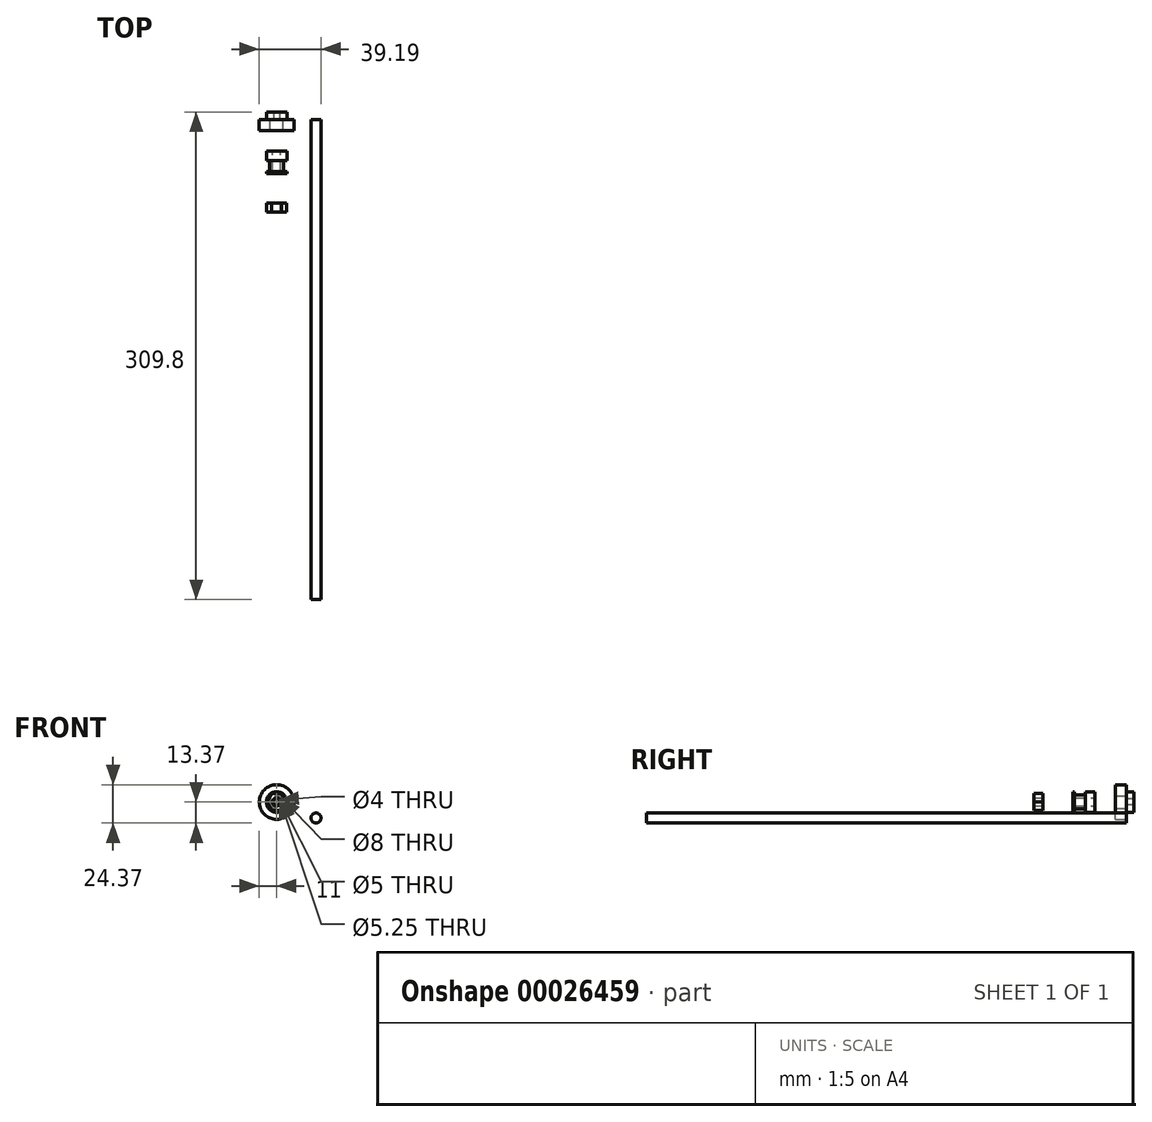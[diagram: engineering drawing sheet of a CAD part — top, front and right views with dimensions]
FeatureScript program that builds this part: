
annotation { "Feature Type Name" : "Feature", "Feature Type Description" : "" }
export const myFeature = defineFeature(function(context is Context, id is Id, definition is map)
    precondition{}
    {
        {
            var Q0;
            Q0=qCreatedBy(makeId("Front.planeOp"),FACE);
            cPlane(context, id + "F0", {"entities" : qUnion([Q0]), "cplaneType" : CPlaneType.OFFSET, "offset" : 20 * mm, "width" : 150 * mm, "height" : 150 * mm});
        }
        {
            var Q0;
            Q0=qCreatedBy(makeId("Front.planeOp"),FACE);
            var sketch = newSketch(context, id + "F1", { "sketchPlane" : qUnion([Q0])});
            skCircle(sketch, "E0", {"center": v(0, 0) * mm, "radius": 4 * mm});
            skCircle(sketch, "E1", {"center": v(0, 0) * mm, "radius": 11 * mm});
            skSolve(sketch);
        }
        {
            var Q0;
            Q0=makeQuery(id+"F1.imprint","IMPRINT",FACE,{"disambiguationData":[TD([[makeQuery(id+"F1.imprint","IMPRINT",EDGE,{"derivedFrom":sQuery(id+"F1.wireOp",EDGE,"E0")}),-1.0]])]});
            var Q1;
            Q1=sQuery(id+"F1.wireOp",EDGE,"E1");
            extrude(context, id + "F14", {"entities" : qUnion([Q0]), "surfaceEntities" : qUnion([Q1]), "depth" : 7 * mm});
        }
        {
            var Q0;
            Q0=qCreatedBy(makeId("Front.planeOp"),FACE);
            var sketch = newSketch(context, id + "F2", { "sketchPlane" : qUnion([Q0])});
            skCircle(sketch, "E2", {"center": v(0, 0) * mm, "radius": 2 * mm});
            skCircle(sketch, "E3", {"center": v(0, 0) * mm, "radius": 6.5 * mm});
            skSolve(sketch);
        }
        {
            var Q0;
            Q0=makeQuery(id+"F2.imprint","IMPRINT",FACE,{"disambiguationData":[TD([[makeQuery(id+"F2.imprint","IMPRINT",EDGE,{"derivedFrom":sQuery(id+"F2.wireOp",EDGE,"E2")}),-1.0]])]});
            extrude(context, id + "F3", {"entities" : qUnion([Q0]), "oppositeDirection" : true, "depth" : 5 * mm});
        }
        {
            var Q0;
            Q0=qCreatedBy(id+"F0.planeOp",FACE);
            var sketch = newSketch(context, id + "F4", { "sketchPlane" : qUnion([Q0])});
            skCircle(sketch, "E4", {"center": v(0, 0) * mm, "radius": 6.5 * mm});
            skCircle(sketch, "E5", {"center": v(0, 0) * mm, "radius": 2.5 * mm});
            skSolve(sketch);
        }
        {
            var Q0;
            Q0=makeQuery(id+"F4.imprint","IMPRINT",FACE,{"disambiguationData":[TD([[makeQuery(id+"F4.imprint","IMPRINT",EDGE,{"derivedFrom":sQuery(id+"F4.wireOp",EDGE,"E4")}),1.0]])]});
            extrude(context, id + "F5", {"entities" : qUnion([Q0]), "depth" : 14 * mm});
        }
        {
            var Q0;
            Q0=makeQuery(id+"F5.opExtrude","CAP_FACE",FACE,{"disambiguationData":[OSD([sQuery(id+"F4.wireOp",EDGE,"E4"),sQuery(id+"F4.wireOp",EDGE,"E5")])],"isStart":false});
            cPlane(context, id + "F6", {"entities" : qUnion([Q0]), "cplaneType" : CPlaneType.OFFSET, "offset" : 1 * mm, "oppositeDirection" : true, "width" : 150 * mm, "height" : 150 * mm});
        }
        {
            var Q0;
            Q0=qCreatedBy(id+"F6.planeOp",FACE);
            var sketch = newSketch(context, id + "F7", { "sketchPlane" : qUnion([Q0])});
            skCircle(sketch, "E6", {"center": v(0, 0) * mm, "radius": 4.5 * mm});
            skCircle(sketch, "E7", {"center": v(0, 0) * mm, "radius": 7.94 * mm});
            skSolve(sketch);
        }
        {
            var Q0;
            Q0=makeQuery(id+"F7.imprint","IMPRINT",FACE,{"disambiguationData":[TD([[makeQuery(id+"F7.imprint","IMPRINT",EDGE,{"derivedFrom":sQuery(id+"F7.wireOp",EDGE,"E6")}),-1.0]])]});
            extrude(context, id + "F8", {"entities" : qUnion([Q0]), "operationType" : NewBodyOperationType.REMOVE, "oppositeDirection" : true, "depth" : 7 * mm});
        }
        {
            var Q0;
            Q0=qCreatedBy(id+"F6.planeOp",FACE);
            cPlane(context, id + "F9", {"entities" : qUnion([Q0]), "cplaneType" : CPlaneType.OFFSET, "offset" : 20 * mm, "width" : 150 * mm, "height" : 150 * mm});
        }
        {
            var Q0;
            Q0=qCreatedBy(id+"F9.planeOp",FACE);
            var sketch = newSketch(context, id + "F10", { "sketchPlane" : qUnion([Q0])});
            skCircle(sketch, "E8", {"center": v(0, 0) * mm, "radius": 2.62 * mm});
            skCircle(sketch, "E9.cCircle", {"center": v(0, 0) * mm, "radius": 5.5 * mm, "construction": true});
            skLineSegment(sketch, "E9.0", {"start": v(3.18, -5.5) * mm, "end": v(-3.18, -5.5) * mm});
            skLineSegment(sketch, "E9.1", {"start": v(-3.18, -5.5) * mm, "end": v(-6.35, 0) * mm});
            skLineSegment(sketch, "E9.2", {"start": v(-6.35, 0) * mm, "end": v(-3.18, 5.5) * mm});
            skLineSegment(sketch, "E9.3", {"start": v(-3.18, 5.5) * mm, "end": v(3.18, 5.5) * mm});
            skLineSegment(sketch, "E9.4", {"start": v(3.18, 5.5) * mm, "end": v(6.35, 0) * mm});
            skLineSegment(sketch, "E9.5", {"start": v(6.35, 0) * mm, "end": v(3.18, -5.5) * mm});
            skPoint(sketch, "E9.0.midPoint", {"position": v(0, -5.5) * mm});
            skSolve(sketch);
        }
        {
            var Q0;
            Q0=makeQuery(id+"F10.imprint","IMPRINT",FACE,{"disambiguationData":[TD([[makeQuery(id+"F10.imprint","IMPRINT",EDGE,{"derivedFrom":sQuery(id+"F10.wireOp",EDGE,"E8")}),-1.0]])]});
            extrude(context, id + "F11", {"entities" : qUnion([Q0]), "depth" : 5.5 * mm});
        }
        {
            var Q0;
            Q0=qCreatedBy(makeId("Front.planeOp"),FACE);
            var sketch = newSketch(context, id + "F12", { "sketchPlane" : qUnion([Q0])});
            skCircle(sketch, "E10", {"center": v(25.01, -10.2) * mm, "radius": 3.18 * mm});
            skSolve(sketch);
        }
        {
            var Q0;
            Q0=makeQuery(id+"F12.imprint","IMPRINT",FACE,{"disambiguationData":[TD([[makeQuery(id+"F12.imprint","IMPRINT",EDGE,{"derivedFrom":sQuery(id+"F12.wireOp",EDGE,"E10")}),1.0]])]});
            extrude(context, id + "F13", {"entities" : qUnion([Q0]), "depth" : 304.8 * mm});
        }
    });
